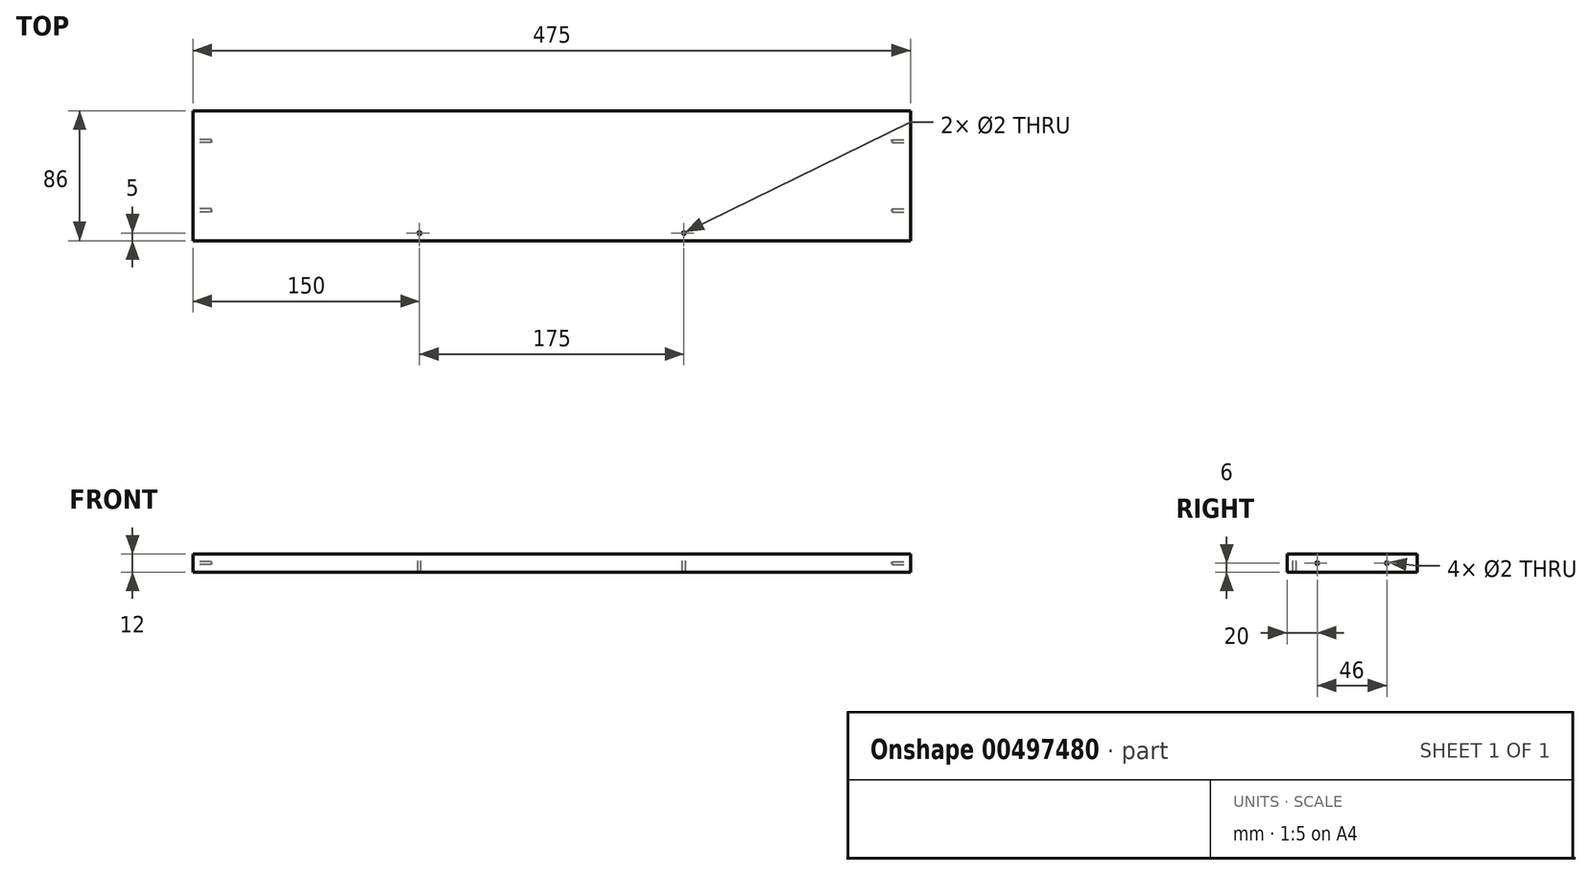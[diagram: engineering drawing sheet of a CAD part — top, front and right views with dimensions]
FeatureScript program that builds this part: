
annotation { "Feature Type Name" : "Feature", "Feature Type Description" : "" }
export const myFeature = defineFeature(function(context is Context, id is Id, definition is map)
    precondition{}
    {
        {
            var Q0;
            Q0=qCreatedBy(makeId("Top.planeOp"),FACE);
            var sketch = newSketch(context, id + "F0", { "sketchPlane" : qUnion([Q0])});
            skLineSegment(sketch, "E0.bottom", {"start": v(0, 0) * mm, "end": v(-237.5, 0) * mm});
            skLineSegment(sketch, "E0.top", {"start": v(0, -43) * mm, "end": v(-237.5, -43) * mm});
            skLineSegment(sketch, "E0.left", {"start": v(0, 0) * mm, "end": v(0, -43) * mm});
            skLineSegment(sketch, "E0.right", {"start": v(-237.5, 0) * mm, "end": v(-237.5, -43) * mm});
            skSolve(sketch);
        }
        {
            var Q0;
            Q0=qSketchRegion(id+"F0",true);
            extrude(context, id + "F1", {"entities" : qUnion([Q0]), "depth" : 12 * mm});
        }
        {
            var Q0;
            Q0=makeQuery(id+"F1.opExtrude","SWEPT_FACE",FACE,{"disambiguationData":[OSD([sQuery(id+"F0.wireOp",EDGE,"E0.right")])]});
            var sketch = newSketch(context, id + "F2", { "sketchPlane" : qUnion([Q0])});
            skPoint(sketch, "E1", {"position": v(43, 6) * mm});
            skPoint(sketch, "E2", {"position": v(23, 6) * mm});
            skSolve(sketch);
        }
        {
            var Q0;
            Q0=sQuery(id+"F2.wireOp",VERTEX,"E2");
            var Q1;
            Q1=makeQuery(id+"F1.opExtrude","SWEPT_BODY",BODY,{"disambiguationData":[OSD([sQuery(id+"F0.wireOp",EDGE,"E0.bottom"),sQuery(id+"F0.wireOp",EDGE,"E0.top"),sQuery(id+"F0.wireOp",EDGE,"E0.left"),sQuery(id+"F0.wireOp",EDGE,"E0.right")])]});
            hole(context, id + "F3", {"style" : HoleStyle.SIMPLE, "endStyle" : HoleEndStyle.BLIND, "holeDiameter" : 2 * mm, "holeDepth" : 12 * mm, "isTappedThrough" : true, "tappedDepth" : 12 * mm, "tapClearance" : 3, "locations" : qUnion([Q0]), "scope" : qUnion([Q1])});
        }
        {
            var Q0;
            Q0=makeQuery(id+"F1.opExtrude","SWEPT_BODY",BODY,{"disambiguationData":[OSD([sQuery(id+"F0.wireOp",EDGE,"E0.bottom"),sQuery(id+"F0.wireOp",EDGE,"E0.top"),sQuery(id+"F0.wireOp",EDGE,"E0.left"),sQuery(id+"F0.wireOp",EDGE,"E0.right")])]});
            var Q1;
            Q1=qCreatedBy(makeId("Front.planeOp"),FACE);
            mirror(context, id + "F4", {"operationType" : NewBodyOperationType.ADD, "entities" : qUnion([Q0]), "mirrorPlane" : qUnion([Q1])});
        }
        {
            var Q0;
            {var subQ0=makeQuery(id+"F1.opExtrude","CAP_FACE",FACE,{"disambiguationData":[OSD([sQuery(id+"F0.wireOp",EDGE,"E0.bottom"),sQuery(id+"F0.wireOp",EDGE,"E0.top"),sQuery(id+"F0.wireOp",EDGE,"E0.left"),sQuery(id+"F0.wireOp",EDGE,"E0.right")])],"isStart":false});var subQ1=makeQuery(id+"F4.boolean.opBoolean","MERGE",FACE,{"derivedFrom":[subQ0,makeQuery(id+"F4.opPattern","COPY",FACE,{"derivedFrom":subQ0,"instanceName":"1"})]});Q0=makeQuery(id+"F7.boolean.opBoolean","MERGE",FACE,{"derivedFrom":[subQ1,makeQuery(id+"F7.opPattern","COPY",FACE,{"derivedFrom":subQ1,"instanceName":"1"})]});}
            var sketch = newSketch(context, id + "F5", { "sketchPlane" : qUnion([Q0])});
            skPoint(sketch, "E3", {"position": v(-87.5, -43) * mm});
            skPoint(sketch, "E4", {"position": v(-87.5, -38) * mm});
            skSolve(sketch);
        }
        {
            var Q0;
            Q0=sQuery(id+"F5.wireOp",VERTEX,"E4");
            var Q1;
            Q1=makeQuery(id+"F1.opExtrude","SWEPT_BODY",BODY,{"disambiguationData":[OSD([sQuery(id+"F0.wireOp",EDGE,"E0.bottom"),sQuery(id+"F0.wireOp",EDGE,"E0.top"),sQuery(id+"F0.wireOp",EDGE,"E0.left"),sQuery(id+"F0.wireOp",EDGE,"E0.right")])]});
            hole(context, id + "F6", {"style" : HoleStyle.SIMPLE, "endStyle" : HoleEndStyle.THROUGH, "holeDiameter" : 2 * mm, "isTappedThrough" : true, "tappedDepth" : 12 * mm, "tapClearance" : 3, "locations" : qUnion([Q0]), "scope" : qUnion([Q1])});
        }
        {
            var Q0;
            Q0=makeQuery(id+"F1.opExtrude","SWEPT_BODY",BODY,{"disambiguationData":[OSD([sQuery(id+"F0.wireOp",EDGE,"E0.bottom"),sQuery(id+"F0.wireOp",EDGE,"E0.top"),sQuery(id+"F0.wireOp",EDGE,"E0.left"),sQuery(id+"F0.wireOp",EDGE,"E0.right")])]});
            var Q1;
            Q1=qCreatedBy(makeId("Right.planeOp"),FACE);
            mirror(context, id + "F7", {"operationType" : NewBodyOperationType.ADD, "entities" : qUnion([Q0]), "mirrorPlane" : qUnion([Q1])});
        }
    });
